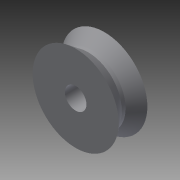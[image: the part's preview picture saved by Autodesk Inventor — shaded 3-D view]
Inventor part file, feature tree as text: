
AUTODESK INVENTOR PART (.ipt)
format: ipt  version: 2013 SP2 (Build 170200200, 200)  size: 89,600 bytes
history: native  units: mm
features: revolve x1, sketch x1
ambient origin geometry x8: Origin, YZ Plane, XZ Plane, XY Plane, X Axis, Y Axis, Z Axis, Center Point
bodies: Solid1 (feature_tree)
feature tree (2):
  revolve  "Revolution1"  [1 undecoded]
  sketch  "Sketch1"  dims[d0=1.5mm d1=4.0mm d2=6.0mm d3=1.5mm d4=90.0deg d5=0.2mm]
note: 1 required parameter value undecoded (feature->parameter linkage not recoverable at this tier; creation-order binding heuristic only, values carry confidence <= 0.55)
